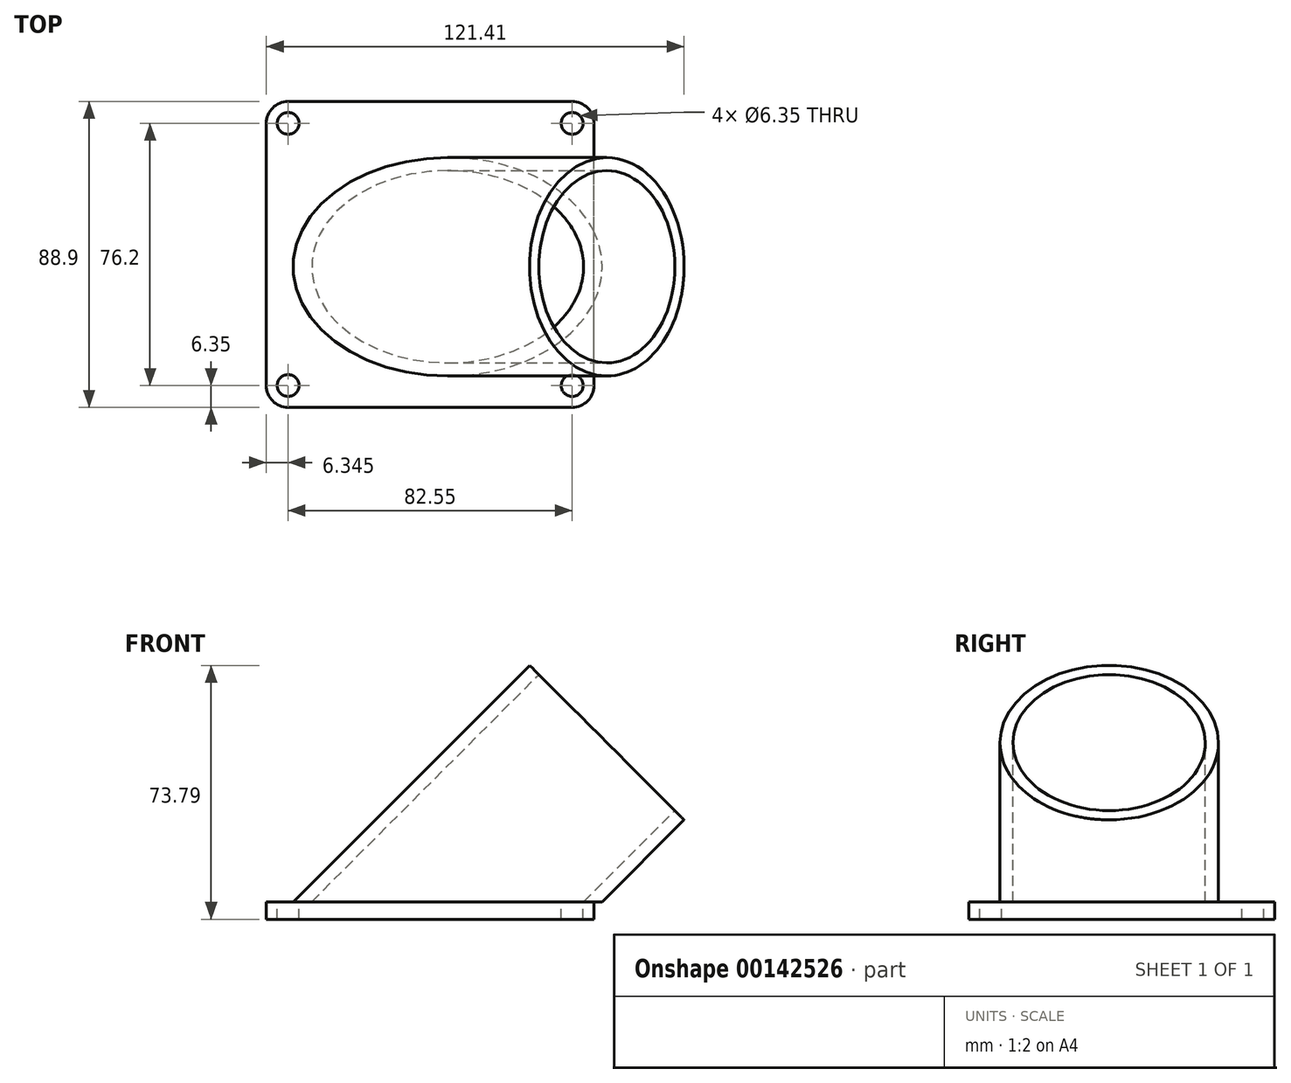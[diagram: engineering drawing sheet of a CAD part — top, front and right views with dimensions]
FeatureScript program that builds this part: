
annotation { "Feature Type Name" : "Feature", "Feature Type Description" : "" }
export const myFeature = defineFeature(function(context is Context, id is Id, definition is map)
    precondition{}
    {
        {
            var Q0;
            Q0=qCreatedBy(makeId("Top.planeOp"),FACE);
            var sketch = newSketch(context, id + "F0", { "sketchPlane" : qUnion([Q0])});
            skLineSegment(sketch, "E0.bottom", {"start": v(47.63, -44.45) * mm, "end": v(-47.62, -44.45) * mm});
            skLineSegment(sketch, "E0.top", {"start": v(47.63, 44.45) * mm, "end": v(-47.62, 44.45) * mm});
            skLineSegment(sketch, "E0.left", {"start": v(47.63, -44.45) * mm, "end": v(47.63, 44.45) * mm});
            skLineSegment(sketch, "E0.right", {"start": v(-47.62, -44.45) * mm, "end": v(-47.62, 44.45) * mm});
            skPoint(sketch, "E0.middle", {"position": v(0, 0) * mm});
            skSolve(sketch);
        }
        {
            var Q0;
            Q0 = qSketchRegion(id + "F0", true);
            extrude(context, id + "F1", {"entities" : qUnion([Q0]), "depth" : 5.08 * mm});
        }
        {
            var Q0;
            Q0=qCreatedBy(makeId("Top.planeOp"),FACE);
            var sketch = newSketch(context, id + "F2", { "sketchPlane" : qUnion([Q0])});
            skLineSegment(sketch, "E1", {"start": v(-5.08, -13.35) * mm, "end": v(-5.08, 13.26) * mm});
            skSolve(sketch);
        }
        {
            var Q0;
            Q0=sQuery(id+"F2.wireOp",EDGE,"E1");
            var Q1;
            Q1=makeQuery(id+"F1.opExtrude","CAP_FACE",FACE,{"disambiguationData":[OSD([sQuery(id+"F0.wireOp",EDGE,"E0.bottom"),sQuery(id+"F0.wireOp",EDGE,"E0.top"),sQuery(id+"F0.wireOp",EDGE,"E0.left"),sQuery(id+"F0.wireOp",EDGE,"E0.right")])],"isStart":true});
            cPlane(context, id + "F3", {"entities" : qUnion([Q0, Q1]), "cplaneType" : CPlaneType.LINE_ANGLE, "offset" : 25.4 * mm, "angle" : 45 * degree, "width" : 152.4 * mm, "height" : 152.4 * mm});
        }
        {
            var Q0;
            Q0=qCreatedBy(id+"F3.planeOp",FACE);
            var sketch = newSketch(context, id + "F4", { "sketchPlane" : qUnion([Q0])});
            skCircle(sketch, "E2", {"center": v(-3.6, 0) * mm, "radius": 31.75 * mm});
            skSolve(sketch);
        }
        {
            var Q0;
            Q0=makeQuery(id+"F4.imprint","IMPRINT",FACE,{"disambiguationData":[TD([[makeQuery(id+"F4.imprint","IMPRINT",EDGE,{"derivedFrom":sQuery(id+"F4.wireOp",EDGE,"E2")}),1.0]])]});
            var Q1;
            Q1=sQuery(id+"F4.wireOp",EDGE,"E2");
            var Q2;
            Q2=makeQuery(id+"F1.opExtrude","CAP_FACE",FACE,{"disambiguationData":[OSD([sQuery(id+"F0.wireOp",EDGE,"E0.bottom"),sQuery(id+"F0.wireOp",EDGE,"E0.top"),sQuery(id+"F0.wireOp",EDGE,"E0.left"),sQuery(id+"F0.wireOp",EDGE,"E0.right")])],"isStart":false});
            extrude(context, id + "F5", {"entities" : qUnion([Q0]), "operationType" : NewBodyOperationType.ADD, "surfaceEntities" : qUnion([Q1]), "depth" : 76.2 * mm, "hasSecondDirection" : true, "secondDirectionBound" : SecondDirectionBoundingType.UP_TO_SURFACE, "secondDirectionOppositeDirection" : true, "secondDirectionBoundEntityFace" : qUnion([Q2]), "secondDirectionDepth" : 25.4 * mm});
        }
        {
            var Q0;
            Q0=makeQuery(id+"F5.opExtrude","CAP_FACE",FACE,{"disambiguationData":[OSD([sQuery(id+"F4.wireOp",EDGE,"E2")])],"isStart":false});
            var sketch = newSketch(context, id + "F6", { "sketchPlane" : qUnion([Q0])});
            skCircle(sketch, "E3", {"center": v(-3.6, 0) * mm, "radius": 27.94 * mm});
            skSolve(sketch);
        }
        {
            var Q0;
            Q0=makeQuery(id+"F6.imprint","IMPRINT",FACE,{"disambiguationData":[TD([[makeQuery(id+"F6.imprint","IMPRINT",EDGE,{"derivedFrom":sQuery(id+"F6.wireOp",EDGE,"E3")}),1.0]])]});
            var Q1;
            {var subQ0=sQuery(id+"F0.wireOp",EDGE,"E0.bottom");var subQ1=sQuery(id+"F0.wireOp",EDGE,"E0.left");var subQ2=sQuery(id+"F0.wireOp",EDGE,"E0.right");Q1=makeQuery(id+"F5.boolean.opBoolean","SPLIT",FACE,{"disambiguationData":[TD([makeQuery(id+"F1.opExtrude","SWEPT_FACE",FACE,{"disambiguationData":[OSD([subQ0])]})])],"derivedFrom":makeQuery(id+"F1.opExtrude","CAP_FACE",FACE,{"disambiguationData":[OSD([subQ0,sQuery(id+"F0.wireOp",EDGE,"E0.top"),subQ1,subQ2])],"isStart":false})});}
            extrude(context, id + "F7", {"entities" : qUnion([Q0]), "operationType" : NewBodyOperationType.REMOVE, "endBound" : BoundingType.UP_TO_SURFACE, "oppositeDirection" : true, "endBoundEntityFace" : qUnion([Q1]), "depth" : 25.4 * mm});
        }
        {
            var Q0;
            Q0=makeQuery(id+"F1.opExtrude","SWEPT_EDGE",EDGE,{"disambiguationData":[OSD([sQuery(id+"F0.wireOp",EDGE,"E0.top"),sQuery(id+"F0.wireOp",EDGE,"E0.left")])]});
            var Q1;
            Q1=makeQuery(id+"F1.opExtrude","SWEPT_EDGE",EDGE,{"disambiguationData":[OSD([sQuery(id+"F0.wireOp",EDGE,"E0.top"),sQuery(id+"F0.wireOp",EDGE,"E0.right")])]});
            var Q2;
            Q2=makeQuery(id+"F1.opExtrude","SWEPT_EDGE",EDGE,{"disambiguationData":[OSD([sQuery(id+"F0.wireOp",EDGE,"E0.bottom"),sQuery(id+"F0.wireOp",EDGE,"E0.left")])]});
            var Q3;
            Q3=makeQuery(id+"F1.opExtrude","SWEPT_EDGE",EDGE,{"disambiguationData":[OSD([sQuery(id+"F0.wireOp",EDGE,"E0.bottom"),sQuery(id+"F0.wireOp",EDGE,"E0.right")])]});
            fillet(context, id + "F8", {"entities" : qUnion([Q0, Q1, Q2, Q3]), "radius" : 6.35 * mm, "tangentPropagation" : true, "allowEdgeOverflow" : false});
        }
        {
            var Q0;
            Q0=makeQuery(id+"F1.opExtrude","CAP_FACE",FACE,{"disambiguationData":[OSD([sQuery(id+"F0.wireOp",EDGE,"E0.bottom"),sQuery(id+"F0.wireOp",EDGE,"E0.top"),sQuery(id+"F0.wireOp",EDGE,"E0.left"),sQuery(id+"F0.wireOp",EDGE,"E0.right")])],"isStart":false});
            var sketch = newSketch(context, id + "F9", { "sketchPlane" : qUnion([Q0])});
            skPoint(sketch, "E4", {"position": v(41.28, 38.1) * mm});
            skPoint(sketch, "E5", {"position": v(-41.27, 38.1) * mm});
            skPoint(sketch, "E6", {"position": v(-41.27, -38.1) * mm});
            skPoint(sketch, "E7", {"position": v(41.28, -38.1) * mm});
            skSolve(sketch);
        }
        {
            var Q0;
            Q0=sQuery(id+"F9.wireOp",VERTEX,"E4");
            var Q1;
            Q1=sQuery(id+"F9.wireOp",VERTEX,"E5");
            var Q2;
            Q2=sQuery(id+"F9.wireOp",VERTEX,"E6");
            var Q3;
            Q3=sQuery(id+"F9.wireOp",VERTEX,"E7");
            var Q4;
            Q4=makeQuery(id+"F1.opExtrude","SWEPT_BODY",BODY,{"disambiguationData":[OSD([sQuery(id+"F0.wireOp",EDGE,"E0.bottom"),sQuery(id+"F0.wireOp",EDGE,"E0.top"),sQuery(id+"F0.wireOp",EDGE,"E0.left"),sQuery(id+"F0.wireOp",EDGE,"E0.right")])]});
            hole(context, id + "F10", {"style" : HoleStyle.SIMPLE, "endStyle" : HoleEndStyle.THROUGH, "holeDiameter" : 6.35 * mm, "locations" : qUnion([Q0, Q1, Q2, Q3]), "scope" : qUnion([Q4]), "isTappedThrough" : true});
        }
    });
